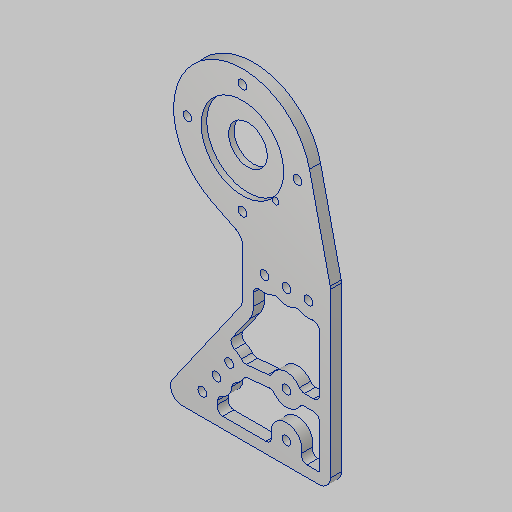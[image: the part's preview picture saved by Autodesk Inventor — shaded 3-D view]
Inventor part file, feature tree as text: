
AUTODESK INVENTOR PART (.ipt)
format: ipt  version: 2023.5 (Build 275446000, 446)  size: 239,616 bytes
history: native  units: in
note: dims shown in document units (in); Inventor stores cm internally (conversion verified against a paired STEP export)
features: other x3, sketch x3
ambient origin geometry x8: Origin, YZ Plane, XZ Plane, XY Plane, X Axis, Y Axis, Z Axis, Center Point
bodies: Solid1 (feature_tree)
feature tree (6):
  other  "CL7-010.ipt"
  other  "Solid1::CL7-010.ipt"
  other  "TaggingFeature1"
  sketch  "Sketch1"  dims[d0=0.3937in]
  sketch  "Sketch2"
  sketch  "Sketch3"
